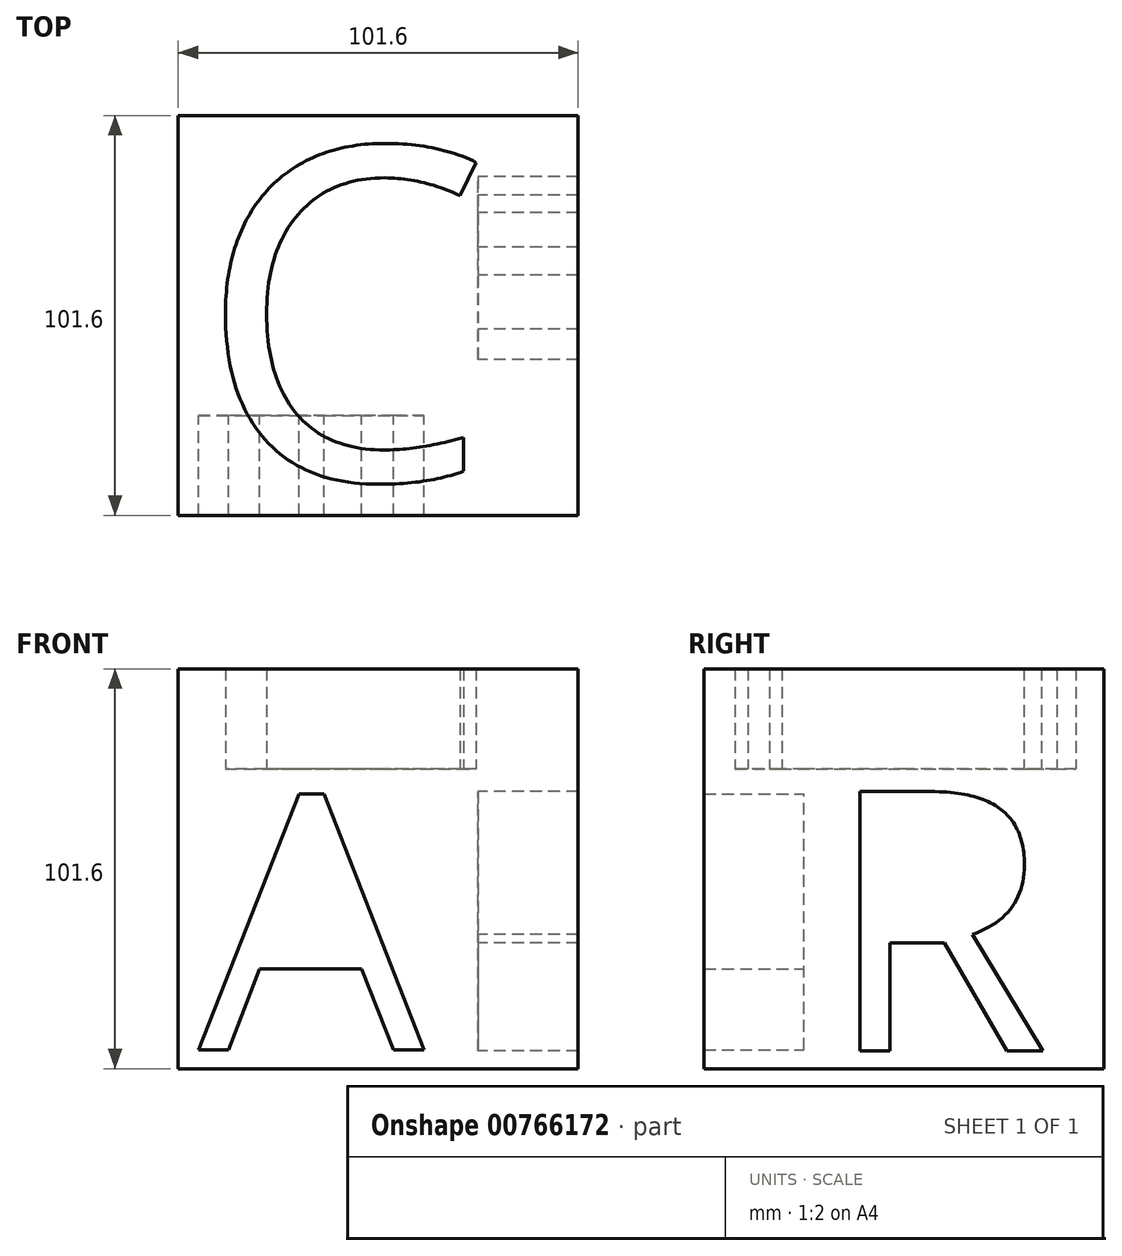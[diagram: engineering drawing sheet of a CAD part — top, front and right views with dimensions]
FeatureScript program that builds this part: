
annotation { "Feature Type Name" : "Feature", "Feature Type Description" : "" }
export const myFeature = defineFeature(function(context is Context, id is Id, definition is map)
    precondition{}
    {
        {
            var Q0;
            Q0=qCreatedBy(makeId("Front.planeOp"),FACE);
            var sketch = newSketch(context, id + "F0", { "sketchPlane" : qUnion([Q0])});
            skLineSegment(sketch, "E0.bottom", {"start": v(-42.6, 47.48) * mm, "end": v(33.6, 47.48) * mm});
            skLineSegment(sketch, "E0.top", {"start": v(-42.6, -28.72) * mm, "end": v(33.6, -28.72) * mm});
            skLineSegment(sketch, "E0.left", {"start": v(-42.6, 47.48) * mm, "end": v(-42.6, -28.72) * mm});
            skLineSegment(sketch, "E0.right", {"start": v(33.6, 47.48) * mm, "end": v(33.6, -28.72) * mm});
            skSolve(sketch);
        }
        {
            var Q0;
            Q0=makeQuery(id+"F0.imprint","IMPRINT",FACE,{"disambiguationData":[TD([[makeQuery(id+"F0.imprint","IMPRINT",EDGE,{"derivedFrom":sQuery(id+"F0.wireOp",EDGE,"E0.bottom")}),-1.0]])]});
            extrude(context, id + "F1", {"entities" : qUnion([Q0]), "depth" : 76.2 * mm, "offsetDistance" : 25.4 * mm});
        }
        {
            var Q0;
            Q0=makeQuery(id+"F1.opExtrude","SWEPT_FACE",FACE,{"disambiguationData":[OSD([sQuery(id+"F0.wireOp",EDGE,"E0.right")])]});
            var sketch = newSketch(context, id + "F2", { "sketchPlane" : qUnion([Q0])});
            skText(sketch, "E1", { "text": "R", "fontName": "OpenSans-Regular.ttf"});
            const initialGuessF2  = {"E1": [-0.07107, -0.02422, 1, 0, 0.06647]};
            skSetInitialGuess(sketch, initialGuessF2);
            skSolve(sketch);
        }
        {
            var Q0;
            Q0=makeQuery(id+"F2.imprint","IMPRINT",FACE,{"disambiguationData":[TD([[makeQuery(id+"F2.imprint","IMPRINT",EDGE,{"derivedFrom":sQuery(id+"F2.wireOp",EDGE,"E1.sketch_text.stroke-0")}),1.0]])]});
            extrude(context, id + "F3", {"entities" : qUnion([Q0]), "operationType" : NewBodyOperationType.ADD, "depth" : 25.4 * mm, "offsetDistance" : 25.4 * mm});
        }
        {
            var Q0;
            {var subQ0=sQuery(id+"F0.wireOp",EDGE,"E0.right");Q0=makeQuery(id+"F3.boolean.opBoolean","MERGE",FACE,{"derivedFrom":[makeQuery(id+"F1.opExtrude","CAP_FACE",FACE,{"disambiguationData":[OSD([sQuery(id+"F0.wireOp",EDGE,"E0.bottom"),sQuery(id+"F0.wireOp",EDGE,"E0.top"),sQuery(id+"F0.wireOp",EDGE,"E0.left"),subQ0])],"isStart":false}),makeQuery(id+"F3.opExtrude","SWEPT_FACE",FACE,{"disambiguationData":[OSD([subQ0]),TDD([makeQuery(id+"F2.imprint","IMPRINT",EDGE,{"derivedFrom":makeQuery(id+"F1.opExtrude","CAP_EDGE",EDGE,{"disambiguationData":[OSD([subQ0])],"isStart":false})})])]})]});}
            var sketch = newSketch(context, id + "F4", { "sketchPlane" : qUnion([Q0])});
            skText(sketch, "E2", { "text": "A", "fontName": "OpenSans-Regular.ttf"});
            const initialGuessF4  = {"E2": [-0.0375, -0.02395, 1, 0, 0.06528]};
            skSetInitialGuess(sketch, initialGuessF4);
            skSolve(sketch);
        }
        {
            var Q0;
            Q0=makeQuery(id+"F4.imprint","IMPRINT",FACE,{"disambiguationData":[TD([[makeQuery(id+"F4.imprint","IMPRINT",EDGE,{"derivedFrom":sQuery(id+"F4.wireOp",EDGE,"E2.sketch_text.stroke-0")}),1.0]])]});
            extrude(context, id + "F5", {"entities" : qUnion([Q0]), "operationType" : NewBodyOperationType.ADD, "depth" : 25.4 * mm, "offsetDistance" : 25.4 * mm});
        }
        {
            var Q0;
            {var subQ0=sQuery(id+"F0.wireOp",EDGE,"E0.right");var subQ1=sQuery(id+"F0.wireOp",EDGE,"E0.bottom");Q0=makeQuery(id+"F5.boolean.opBoolean","MERGE",FACE,{"derivedFrom":[makeQuery(id+"F3.boolean.opBoolean","MERGE",FACE,{"derivedFrom":[makeQuery(id+"F1.opExtrude","SWEPT_FACE",FACE,{"disambiguationData":[OSD([subQ1])]}),makeQuery(id+"F3.opExtrude","SWEPT_FACE",FACE,{"disambiguationData":[OSD([subQ1,subQ0])]})]}),makeQuery(id+"F5.opExtrude","SWEPT_FACE",FACE,{"disambiguationData":[OSD([subQ1,subQ0])]})]});}
            var sketch = newSketch(context, id + "F6", { "sketchPlane" : qUnion([Q0])});
            skText(sketch, "E3", { "text": "C", "fontName": "OpenSans-Regular.ttf"});
            const initialGuessF6  = {"E3": [-0.03782, -0.09255, 1, 0, 0.08496]};
            skSetInitialGuess(sketch, initialGuessF6);
            skSolve(sketch);
        }
        {
            var Q0;
            Q0=makeQuery(id+"F6.imprint","IMPRINT",FACE,{"disambiguationData":[TD([[makeQuery(id+"F6.imprint","IMPRINT",EDGE,{"derivedFrom":sQuery(id+"F6.wireOp",EDGE,"E3.sketch_text.stroke-0")}),1.0]])]});
            extrude(context, id + "F7", {"entities" : qUnion([Q0]), "operationType" : NewBodyOperationType.ADD, "depth" : 25.4 * mm, "offsetDistance" : 25.4 * mm});
        }
    });
